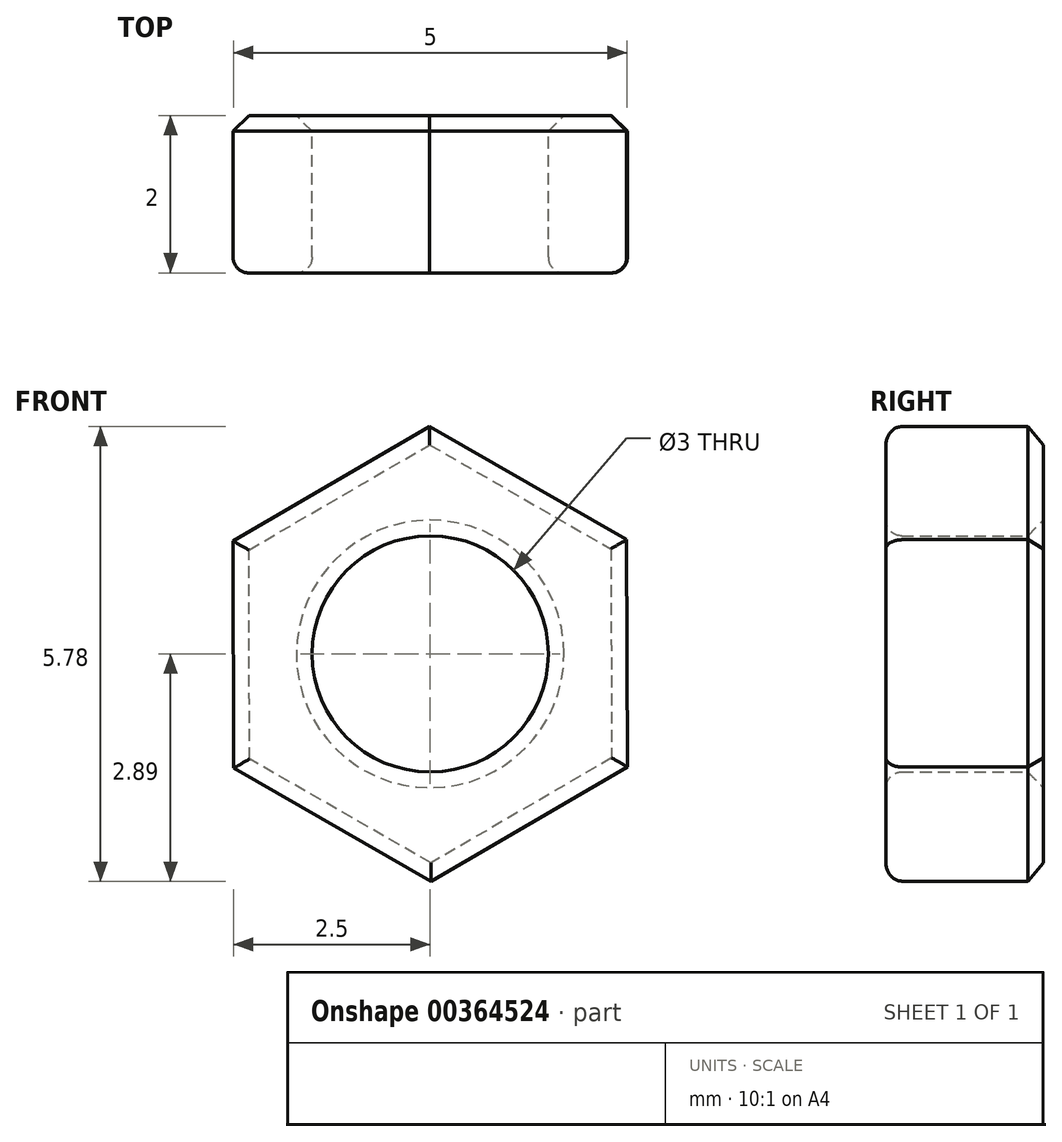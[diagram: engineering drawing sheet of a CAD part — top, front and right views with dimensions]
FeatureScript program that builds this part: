
annotation { "Feature Type Name" : "Feature", "Feature Type Description" : "" }
export const myFeature = defineFeature(function(context is Context, id is Id, definition is map)
    precondition{}
    {
        {
            var Q0;
            Q0=qCreatedBy(makeId("Front.planeOp"),FACE);
            var sketch = newSketch(context, id + "F0", { "sketchPlane" : qUnion([Q0])});
            skCircle(sketch, "E0.cCircle", {"center": v(0, 0) * mm, "radius": 2.5 * mm, "construction": true});
            skLineSegment(sketch, "E0.0", {"start": v(0, 2.89) * mm, "end": v(2.5, 1.45) * mm});
            skLineSegment(sketch, "E0.1", {"start": v(2.5, 1.45) * mm, "end": v(2.5, -1.44) * mm});
            skLineSegment(sketch, "E0.2", {"start": v(2.5, -1.44) * mm, "end": v(0, -2.89) * mm});
            skLineSegment(sketch, "E0.3", {"start": v(0, -2.89) * mm, "end": v(-2.5, -1.45) * mm});
            skLineSegment(sketch, "E0.4", {"start": v(-2.5, -1.45) * mm, "end": v(-2.5, 1.44) * mm});
            skLineSegment(sketch, "E0.5", {"start": v(-2.5, 1.44) * mm, "end": v(0, 2.89) * mm});
            skPoint(sketch, "E0.0.midPoint", {"position": v(1.24, 2.17) * mm});
            skCircle(sketch, "E1", {"center": v(0, 0) * mm, "radius": 1.5 * mm});
            skSolve(sketch);
        }
        {
            var Q0;
            Q0=makeQuery(id+"F0.imprint","IMPRINT",FACE,{"disambiguationData":[TD([[makeQuery(id+"F0.imprint","IMPRINT",EDGE,{"derivedFrom":sQuery(id+"F0.wireOp",EDGE,"E0.0")}),-1.0]])]});
            extrude(context, id + "F1", {"entities" : qUnion([Q0]), "depth" : 2 * mm});
        }
        {
            var Q0;
            Q0=makeQuery(id+"F1.opExtrude","CAP_FACE",FACE,{"disambiguationData":[OSD([sQuery(id+"F0.wireOp",EDGE,"E0.0"),sQuery(id+"F0.wireOp",EDGE,"E0.1"),sQuery(id+"F0.wireOp",EDGE,"E0.2"),sQuery(id+"F0.wireOp",EDGE,"E0.3"),sQuery(id+"F0.wireOp",EDGE,"E0.4"),sQuery(id+"F0.wireOp",EDGE,"E0.5"),sQuery(id+"F0.wireOp",EDGE,"E1")])],"isStart":false});
            fillet(context, id + "F2", {"entities" : qUnion([Q0]), "radius" : 0.2 * mm, "tangentPropagation" : true, "allowEdgeOverflow" : false});
        }
        {
            var Q0;
            Q0=makeQuery(id+"F1.opExtrude","CAP_FACE",FACE,{"disambiguationData":[OSD([sQuery(id+"F0.wireOp",EDGE,"E0.0"),sQuery(id+"F0.wireOp",EDGE,"E0.1"),sQuery(id+"F0.wireOp",EDGE,"E0.2"),sQuery(id+"F0.wireOp",EDGE,"E0.3"),sQuery(id+"F0.wireOp",EDGE,"E0.4"),sQuery(id+"F0.wireOp",EDGE,"E0.5"),sQuery(id+"F0.wireOp",EDGE,"E1")])],"isStart":true});
            chamfer(context, id + "F3", {"entities" : qUnion([Q0]), "width" : 0.2 * mm, "tangentPropagation" : true});
        }
    });
